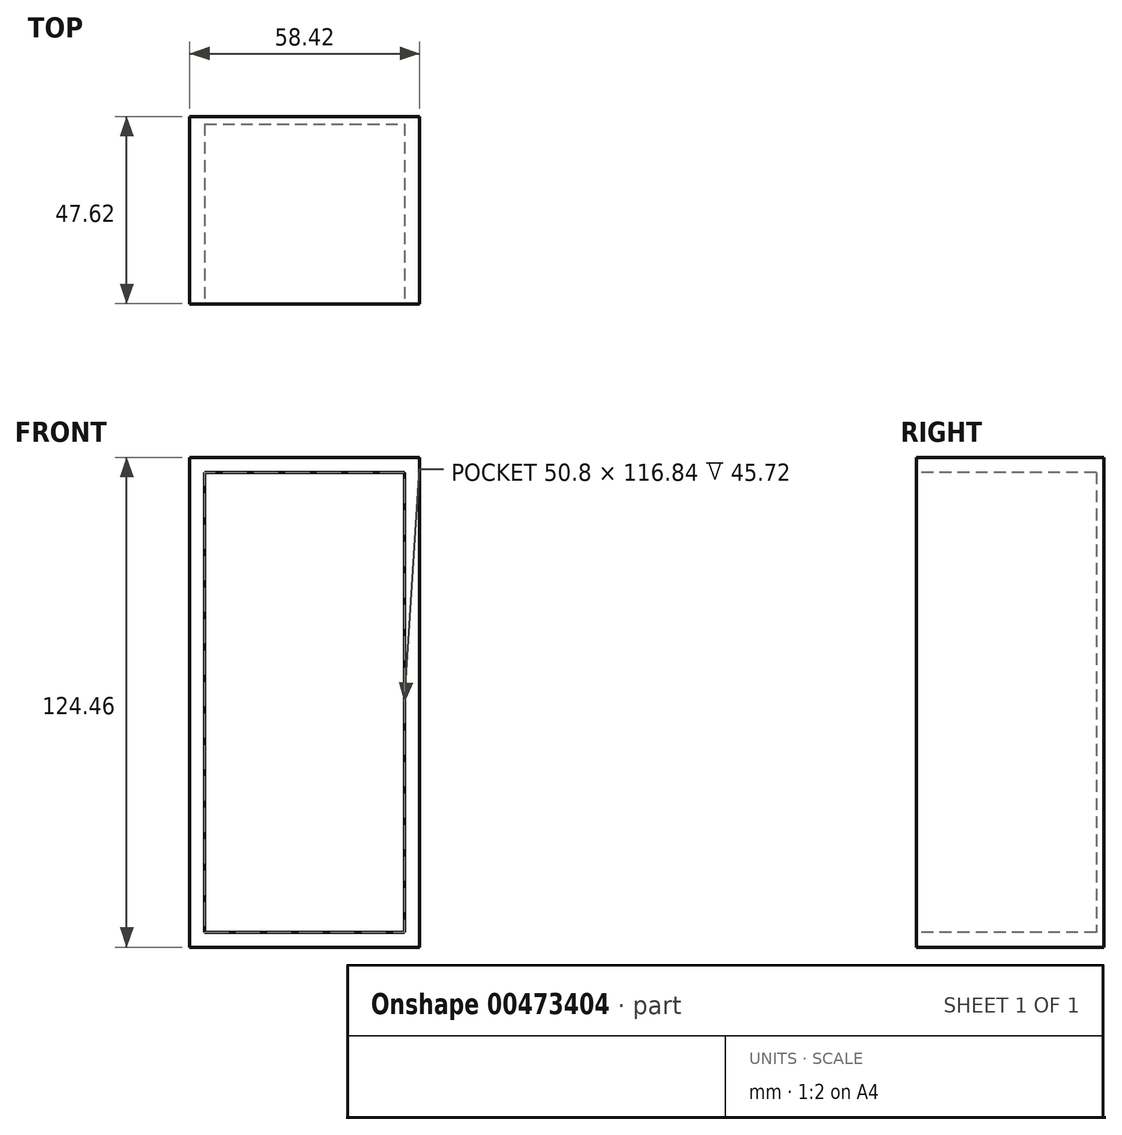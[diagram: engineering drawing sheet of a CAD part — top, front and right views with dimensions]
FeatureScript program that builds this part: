
annotation { "Feature Type Name" : "Feature", "Feature Type Description" : "" }
export const myFeature = defineFeature(function(context is Context, id is Id, definition is map)
    precondition{}
    {
        {
            var Q0;
            Q0=qCreatedBy(makeId("Front.planeOp"),FACE);
            var sketch = newSketch(context, id + "F0", { "sketchPlane" : qUnion([Q0])});
            skLineSegment(sketch, "E0.bottom", {"start": v(-58.73, 124.46) * mm, "end": v(-0.3, 124.46) * mm});
            skLineSegment(sketch, "E0.top", {"start": v(-58.73, 0) * mm, "end": v(-0.3, 0) * mm});
            skLineSegment(sketch, "E0.left", {"start": v(-58.73, 124.46) * mm, "end": v(-58.73, 0) * mm});
            skLineSegment(sketch, "E0.right", {"start": v(-0.3, 124.46) * mm, "end": v(-0.3, 0) * mm});
            skSolve(sketch);
        }
        {
            var Q0;
            Q0=makeQuery(id+"F0.imprint","IMPRINT",FACE,{"disambiguationData":[TD([[makeQuery(id+"F0.imprint","IMPRINT",EDGE,{"derivedFrom":sQuery(id+"F0.wireOp",EDGE,"E0.bottom")}),-1.0]])]});
            extrude(context, id + "F1", {"entities" : qUnion([Q0]), "depth" : 47.62 * mm});
        }
        {
            var Q0;
            Q0=makeQuery(id+"F1.opExtrude","CAP_FACE",FACE,{"disambiguationData":[OSD([sQuery(id+"F0.wireOp",EDGE,"E0.bottom"),sQuery(id+"F0.wireOp",EDGE,"E0.top"),sQuery(id+"F0.wireOp",EDGE,"E0.left"),sQuery(id+"F0.wireOp",EDGE,"E0.right")])],"isStart":false});
            var sketch = newSketch(context, id + "F2", { "sketchPlane" : qUnion([Q0])});
            skLineSegment(sketch, "E1", {"start": v(-48.44, 124.46) * mm, "end": v(-48.44, 120.65) * mm});
            skLineSegment(sketch, "E2", {"start": v(-58.73, 110.15) * mm, "end": v(-54.92, 110.15) * mm});
            skLineSegment(sketch, "E3", {"start": v(-48.44, 0) * mm, "end": v(-48.44, 3.81) * mm});
            skLineSegment(sketch, "E4", {"start": v(-0.3, 32.37) * mm, "end": v(-4.12, 32.37) * mm});
            skLineSegment(sketch, "E5", {"start": v(-48.44, 120.65) * mm, "end": v(-54.92, 120.65) * mm});
            skLineSegment(sketch, "E6", {"start": v(-54.92, 120.65) * mm, "end": v(-54.92, 110.15) * mm});
            skLineSegment(sketch, "E7.bottom", {"start": v(-54.92, 120.65) * mm, "end": v(-4.12, 120.65) * mm});
            skLineSegment(sketch, "E7.top", {"start": v(-54.92, 3.81) * mm, "end": v(-4.12, 3.81) * mm});
            skLineSegment(sketch, "E7.left", {"start": v(-54.92, 120.65) * mm, "end": v(-54.92, 3.81) * mm});
            skLineSegment(sketch, "E7.right", {"start": v(-4.12, 120.65) * mm, "end": v(-4.12, 3.81) * mm});
            skSolve(sketch);
        }
        {
            var Q0;
            {var subQ6=sQuery(id+"F2.wireOp",EDGE,"E7.bottom");var subQ7=makeQuery(id+"F2.imprint","INTERSECT",VERTEX,{"derivedFrom":[sQuery(id+"F2.wireOp",EDGE,"E1"),subQ6]});Q0=makeQuery(id+"F2.imprint","IMPRINT",FACE,{"disambiguationData":[TD([[makeQuery(id+"F2.imprint","IMPRINT",EDGE,{"disambiguationData":[TD([[subQ7,1.0]])],"derivedFrom":subQ6}),-1.0]])]});}
            extrude(context, id + "F3", {"entities" : qUnion([Q0]), "operationType" : NewBodyOperationType.REMOVE, "oppositeDirection" : true, "depth" : 45.72 * mm});
        }
    });
